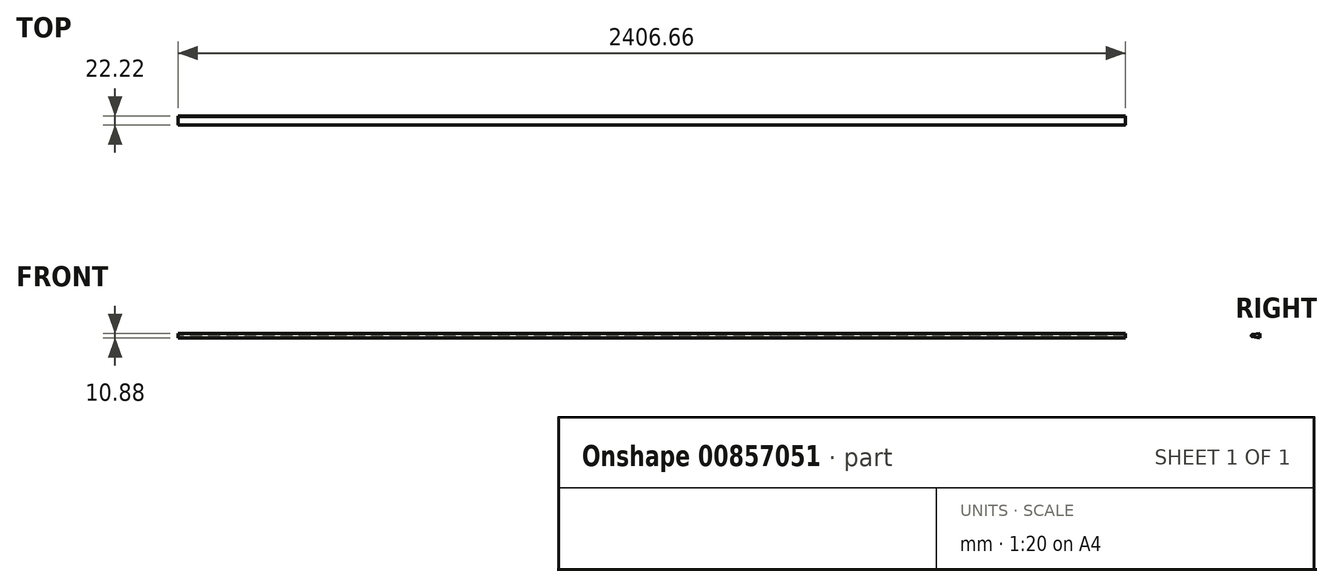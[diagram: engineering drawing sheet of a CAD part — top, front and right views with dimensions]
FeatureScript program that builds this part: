
annotation { "Feature Type Name" : "Feature", "Feature Type Description" : "" }
export const myFeature = defineFeature(function(context is Context, id is Id, definition is map)
    precondition{}
    {
        {
            var Q0;
            Q0=qCreatedBy(makeId("Right.planeOp"),FACE);
            var sketch = newSketch(context, id + "F0", { "sketchPlane" : qUnion([Q0])});
            skLineSegment(sketch, "E0", {"start": v(0, 5.56) * mm, "end": v(0, -5.56) * mm});
            skCircle(sketch, "E1", {"center": v(-19.45, 0) * mm, "radius": 2.78 * mm});
            skLineSegment(sketch, "E2", {"start": v(0, 5.56) * mm, "end": v(-19.84, 2.75) * mm});
            skLineSegment(sketch, "E3", {"start": v(0, -5.56) * mm, "end": v(-19.84, -2.75) * mm});
            skLineSegment(sketch, "E4", {"start": v(-0.85, 5.44) * mm, "end": v(0, 0) * mm});
            skLineSegment(sketch, "E5", {"start": v(0, 0) * mm, "end": v(-0.85, -5.44) * mm});
            skSolve(sketch);
        }
        {
            var Q0;
            {var subQ0=sQuery(id+"F0.wireOp",EDGE,"E1");var subQ1=makeQuery(id+"F0.imprint","INTERSECT",VERTEX,{"derivedFrom":[subQ0,sQuery(id+"F0.wireOp",EDGE,"E2")]});Q0=makeQuery(id+"F0.imprint","IMPRINT",FACE,{"disambiguationData":[TD([[makeQuery(id+"F0.imprint","IMPRINT",EDGE,{"disambiguationData":[TD([[subQ1,-1.0]])],"derivedFrom":subQ0}),1.0]])]});}
            var Q1;
            {var subQ6=sQuery(id+"F0.wireOp",EDGE,"E4");Q1=makeQuery(id+"F0.imprint","IMPRINT",FACE,{"disambiguationData":[TD([[makeQuery(id+"F0.imprint","IMPRINT",EDGE,{"derivedFrom":subQ6}),-1.0]])]});}
            extrude(context, id + "F1", {"entities" : qUnion([Q0, Q1]), "depth" : 2406.65 * mm, "offsetDistance" : 25.4 * mm, "symmetric" : true});
        }
    });
